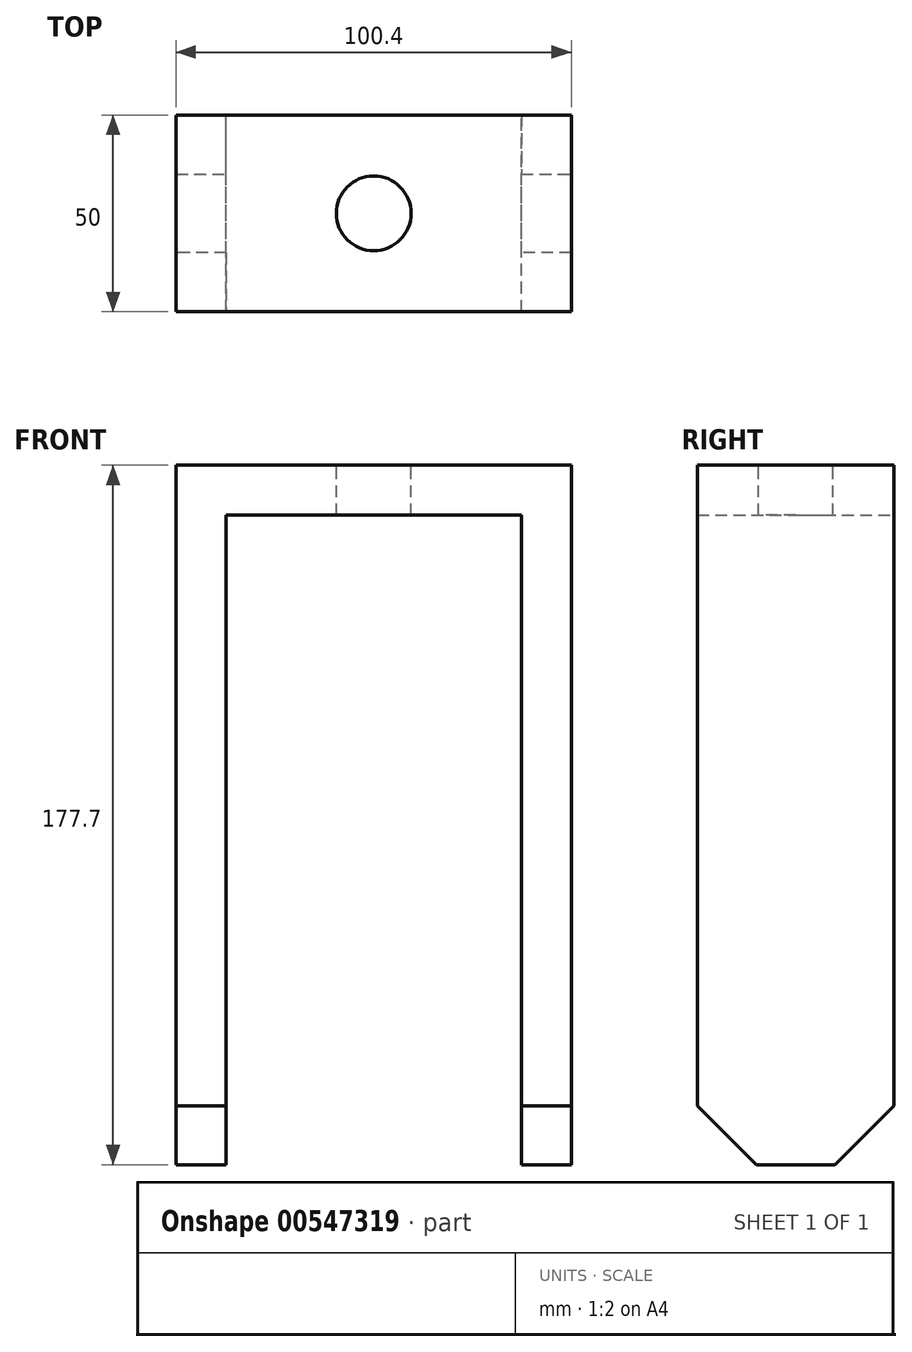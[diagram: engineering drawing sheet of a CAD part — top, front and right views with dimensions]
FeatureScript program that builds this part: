
annotation { "Feature Type Name" : "Feature", "Feature Type Description" : "" }
export const myFeature = defineFeature(function(context is Context, id is Id, definition is map)
    precondition{}
    {
        {
            var Q0;
            Q0=qCreatedBy(makeId("Front.planeOp"),FACE);
            var sketch = newSketch(context, id + "F0", { "sketchPlane" : qUnion([Q0])});
            skLineSegment(sketch, "E0", {"start": v(0, 0) * mm, "end": v(0, 177.7) * mm});
            skLineSegment(sketch, "E1", {"start": v(0, 177.7) * mm, "end": v(100.4, 177.7) * mm});
            skLineSegment(sketch, "E2", {"start": v(100.4, 177.7) * mm, "end": v(100.4, 0) * mm});
            skLineSegment(sketch, "E3", {"start": v(100.4, 0) * mm, "end": v(87.7, 0) * mm});
            skLineSegment(sketch, "E4", {"start": v(87.7, 0) * mm, "end": v(87.7, 165) * mm});
            skLineSegment(sketch, "E5", {"start": v(87.7, 165) * mm, "end": v(12.7, 165) * mm});
            skLineSegment(sketch, "E6", {"start": v(12.7, 165) * mm, "end": v(12.7, 0) * mm});
            skLineSegment(sketch, "E7", {"start": v(12.7, 0) * mm, "end": v(0, 0) * mm});
            skSolve(sketch);
        }
        {
            var Q0;
            Q0 = qSketchRegion(id + "F0", true);
            extrude(context, id + "F1", {"entities" : qUnion([Q0]), "depth" : 50 * mm, "offsetDistance" : 25 * mm});
        }
        {
            var Q0;
            Q0=makeQuery(id+"F1.opExtrude","SWEPT_FACE",FACE,{"disambiguationData":[OSD([sQuery(id+"F0.wireOp",EDGE,"E1")])]});
            var sketch = newSketch(context, id + "F2", { "sketchPlane" : qUnion([Q0])});
            skCircle(sketch, "E8", {"center": v(50.2, -25) * mm, "radius": 9.5 * mm});
            skPoint(sketch, "E8.centerSnap0", {"position": v(100.4, -25) * mm});
            skPoint(sketch, "E8.centerSnap1", {"position": v(50.2, -50) * mm});
            skSolve(sketch);
        }
        {
            var Q0;
            Q0 = qSketchRegion(id + "F2", true);
            extrude(context, id + "F3", {"entities" : qUnion([Q0]), "operationType" : NewBodyOperationType.REMOVE, "endBound" : BoundingType.THROUGH_ALL, "oppositeDirection" : true, "depth" : 25 * mm, "offsetDistance" : 25 * mm});
        }
        {
            var Q0;
            Q0=qCreatedBy(makeId("Right.planeOp"),FACE);
            var sketch = newSketch(context, id + "F4", { "sketchPlane" : qUnion([Q0])});
            skLineSegment(sketch, "E9", {"start": v(-40, 0) * mm, "end": v(-149.7, 113.96) * mm});
            skLineSegment(sketch, "E10", {"start": v(-149.7, 113.96) * mm, "end": v(-149.7, 0) * mm});
            skLineSegment(sketch, "E11", {"start": v(-149.7, 0) * mm, "end": v(-40, 0) * mm});
            skSolve(sketch);
        }
        {
            var Q0;
            Q0=makeQuery(id+"F1.opExtrude","CAP_EDGE",EDGE,{"disambiguationData":[OSD([sQuery(id+"F0.wireOp",EDGE,"E7")])],"isStart":false});
            var Q1;
            Q1=makeQuery(id+"F1.opExtrude","CAP_EDGE",EDGE,{"disambiguationData":[OSD([sQuery(id+"F0.wireOp",EDGE,"E7")])],"isStart":true});
            chamfer(context, id + "F5", {"entities" : qUnion([Q0, Q1]), "width" : 15 * mm, "tangentPropagation" : true});
        }
        {
            var Q0;
            Q0=makeQuery(id+"F1.opExtrude","CAP_EDGE",EDGE,{"disambiguationData":[OSD([sQuery(id+"F0.wireOp",EDGE,"E3")])],"isStart":false});
            var Q1;
            Q1=makeQuery(id+"F1.opExtrude","CAP_EDGE",EDGE,{"disambiguationData":[OSD([sQuery(id+"F0.wireOp",EDGE,"E3")])],"isStart":true});
            chamfer(context, id + "F6", {"entities" : qUnion([Q0, Q1]), "width" : 15 * mm, "tangentPropagation" : true});
        }
    });
